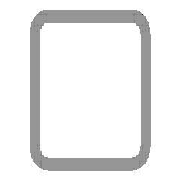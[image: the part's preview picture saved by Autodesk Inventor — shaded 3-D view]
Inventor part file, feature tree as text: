
AUTODESK INVENTOR PART (.ipt)
format: ipt  version: 2025 (Build 290162010, 162A)  size: 134,144 bytes
history: native  units: mm (DEFAULTED — no unit token found)
features: other x4, sketch x1, plane x1
ambient origin geometry x8: Origin, YZ Plane, XZ Plane, XY Plane, X Axis, Y Axis, Z Axis, Center Point
bodies: Solid1 (feature_tree), Body (feature_tree)
feature tree (6):
  parser-record x1  (decoder bookkeeping rows leaked as tree rows — omitted from the tree; the rows remain in map.json)
  other  "Driven Length"
  other  "Start Plane"
  other  "End Plane"
  sketch  "Sketch3"  dims[d3=5000.0mm d4=0.0mm d7=6.0mm d9=100.0mm d11=100.0mm d12=3.0mm d13=-0.0mm d14=5000.0mm d15=50.0mm d16=50.0mm d17=90.0deg d18=5000.0mm]
  plane  "Work Plane3"
